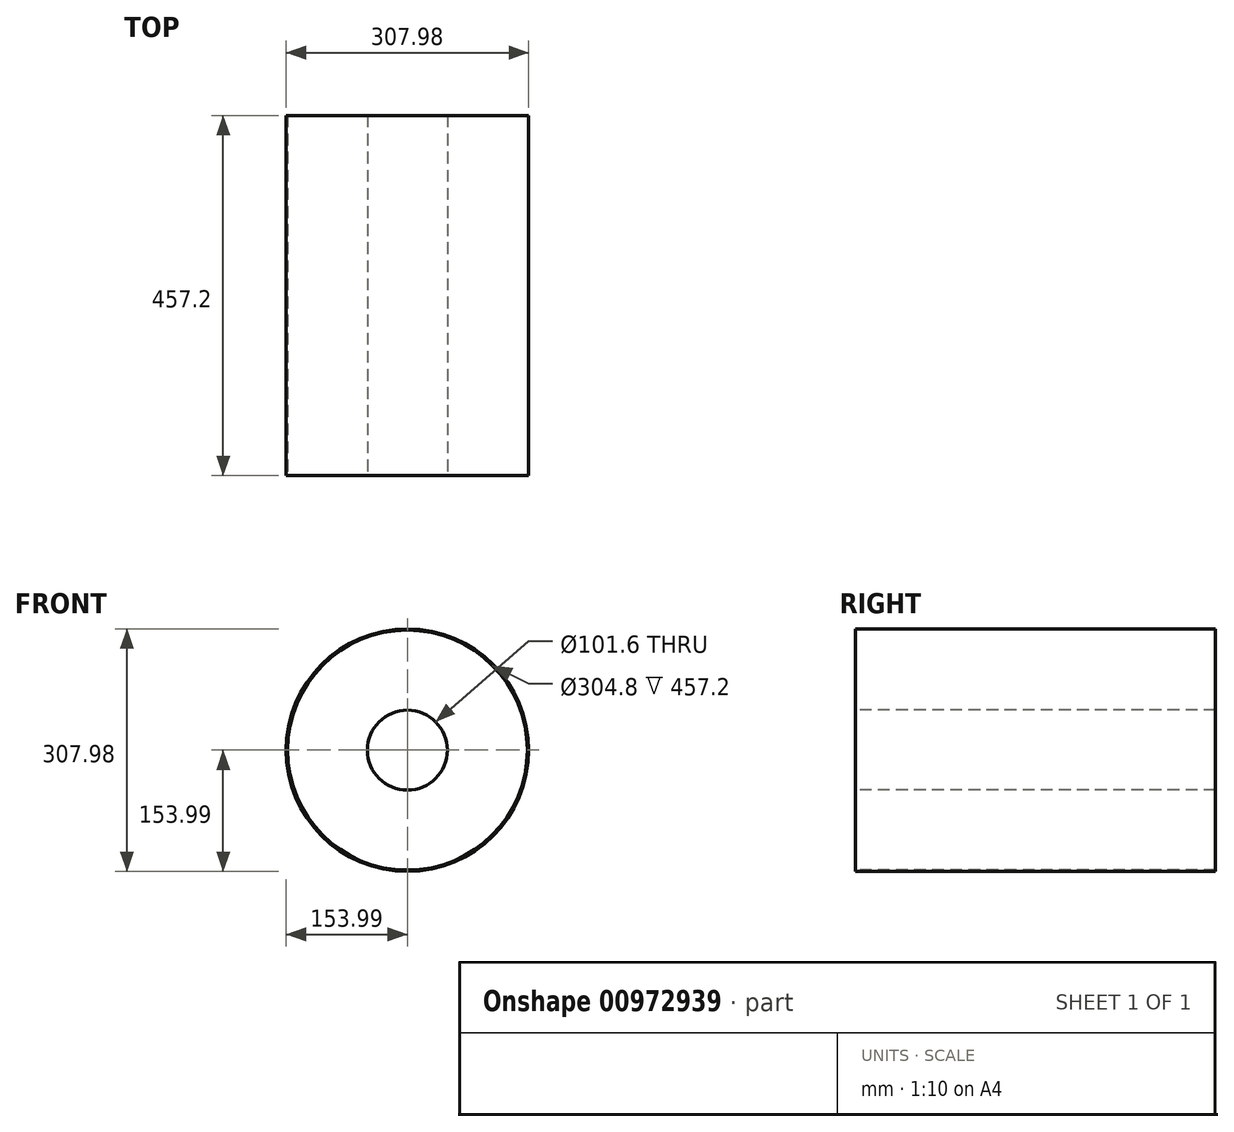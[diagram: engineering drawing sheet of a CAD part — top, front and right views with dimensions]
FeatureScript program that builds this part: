
annotation { "Feature Type Name" : "Feature", "Feature Type Description" : "" }
export const myFeature = defineFeature(function(context is Context, id is Id, definition is map)
    precondition{}
    {
        {
            var Q0;
            Q0=qCreatedBy(makeId("Front.planeOp"),FACE);
            var sketch = newSketch(context, id + "F0", { "sketchPlane" : qUnion([Q0])});
            skCircle(sketch, "E0", {"center": v(0, 0) * mm, "radius": 50.8 * mm});
            skCircle(sketch, "E1", {"center": v(0, 0) * mm, "radius": 152.4 * mm});
            skCircle(sketch, "E2", {"center": v(0, 0) * mm, "radius": 153.99 * mm});
            skSolve(sketch);
        }
        {
            var Q0;
            Q0=makeQuery(id+"F0.imprint","IMPRINT",FACE,{"disambiguationData":[TD([[makeQuery(id+"F0.imprint","IMPRINT",EDGE,{"derivedFrom":sQuery(id+"F0.wireOp",EDGE,"E1")}),-1.0]])]});
            extrude(context, id + "F1", {"entities" : qUnion([Q0]), "oppositeDirection" : true, "depth" : 457.2 * mm, "offsetDistance" : 25.4 * mm});
        }
        {
            var Q0;
            Q0=makeQuery(id+"F0.imprint","IMPRINT",FACE,{"disambiguationData":[TD([[makeQuery(id+"F0.imprint","IMPRINT",EDGE,{"derivedFrom":sQuery(id+"F0.wireOp",EDGE,"E0")}),-1.0]])]});
            extrude(context, id + "F2", {"entities" : qUnion([Q0]), "oppositeDirection" : true, "depth" : 457.2 * mm, "offsetDistance" : 25.4 * mm});
        }
    });
